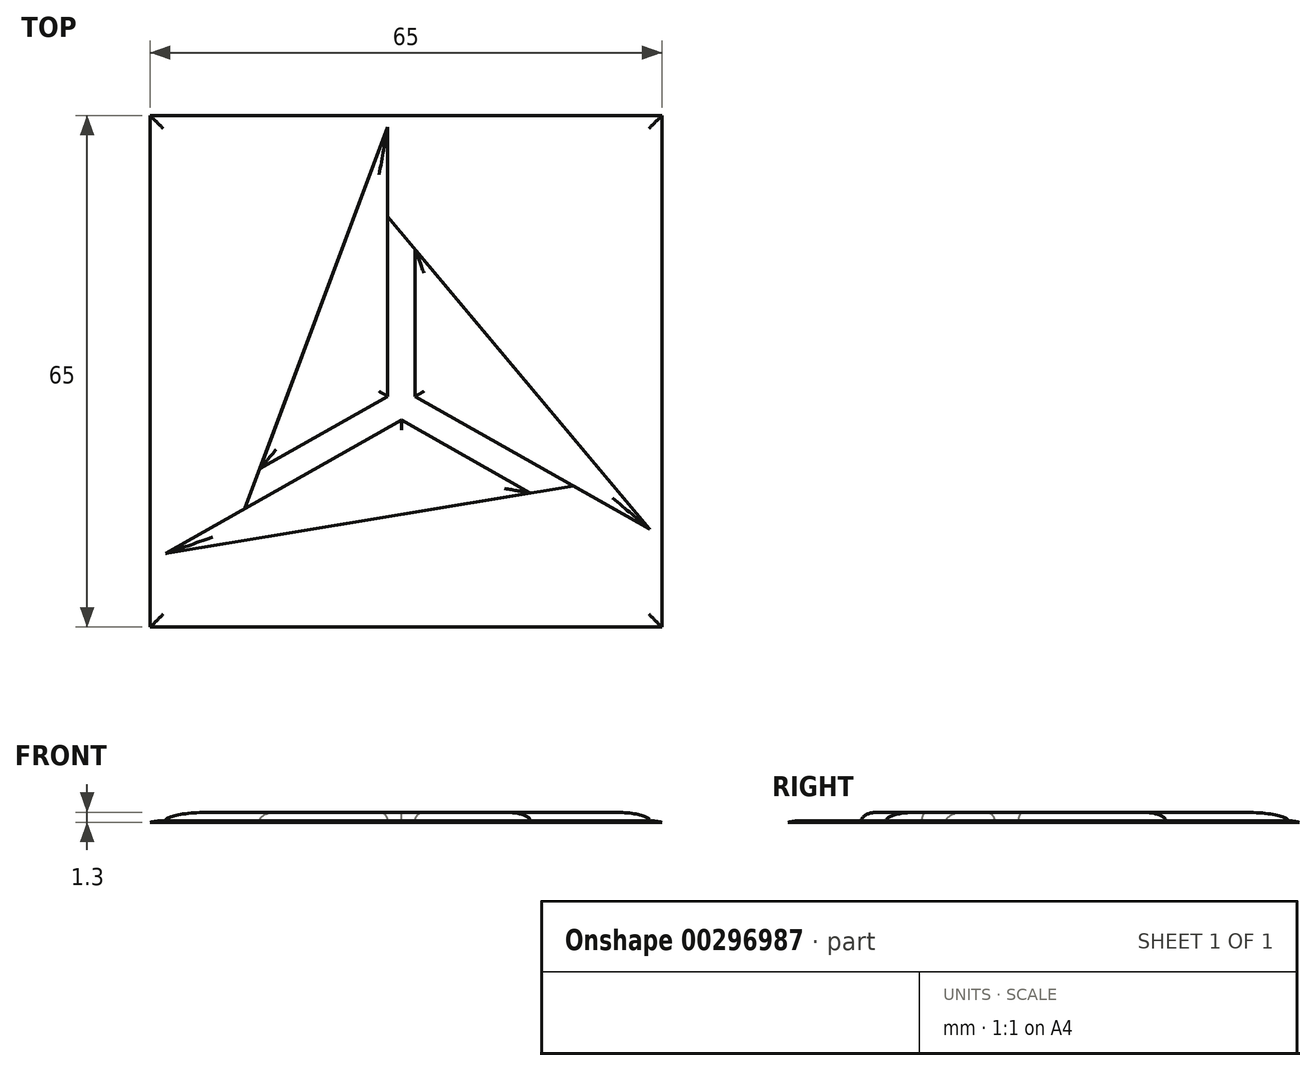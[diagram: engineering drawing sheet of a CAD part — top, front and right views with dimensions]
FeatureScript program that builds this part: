
annotation { "Feature Type Name" : "Feature", "Feature Type Description" : "" }
export const myFeature = defineFeature(function(context is Context, id is Id, definition is map)
    precondition{}
    {
        {
            var Q0;
            Q0=qCreatedBy(makeId("Top.planeOp"),FACE);
            var sketch = newSketch(context, id + "F0", { "sketchPlane" : qUnion([Q0])});
            skLineSegment(sketch, "E0.0", {"start": v(-40.27, 11.94) * mm, "end": v(-24.02, 55.35) * mm});
            skLineSegment(sketch, "E0.1", {"start": v(-24.02, 21.13) * mm, "end": v(-40.27, 11.94) * mm});
            skLineSegment(sketch, "E0.2", {"start": v(-24.02, 55.35) * mm, "end": v(-24.02, 21.13) * mm});
            skLineSegment(sketch, "E1.0", {"start": v(-20.52, 39.8) * mm, "end": v(9.26, 4.28) * mm});
            skLineSegment(sketch, "E1.1", {"start": v(-20.52, 21.13) * mm, "end": v(-20.52, 39.8) * mm});
            skLineSegment(sketch, "E1.2", {"start": v(9.26, 4.28) * mm, "end": v(-20.52, 21.13) * mm});
            skLineSegment(sketch, "E2.0", {"start": v(-5.92, 8.85) * mm, "end": v(-52.25, 1.13) * mm});
            skLineSegment(sketch, "E2.1", {"start": v(-22.27, 18.1) * mm, "end": v(-5.92, 8.85) * mm});
            skLineSegment(sketch, "E2.2", {"start": v(-52.25, 1.13) * mm, "end": v(-22.27, 18.1) * mm});
            skSolve(sketch);
        }
        {
            var Q0;
            Q0=qSketchRegion(id+"F0",true);
            extrude(context, id + "F1", {"entities" : qUnion([Q0]), "depth" : 1.3 * mm, "offsetDistance" : 25 * mm});
        }
        {
            var Q0;
            Q0=makeQuery(id+"F1.opExtrude","CAP_FACE",FACE,{"disambiguationData":[OSD([sQuery(id+"F0.wireOp",EDGE,"E0.0"),sQuery(id+"F0.wireOp",EDGE,"E0.1"),sQuery(id+"F0.wireOp",EDGE,"E0.2")])],"isStart":false});
            var Q1;
            Q1=makeQuery(id+"F1.opExtrude","CAP_FACE",FACE,{"disambiguationData":[OSD([sQuery(id+"F0.wireOp",EDGE,"E1.0"),sQuery(id+"F0.wireOp",EDGE,"E1.1"),sQuery(id+"F0.wireOp",EDGE,"E1.2")])],"isStart":false});
            var Q2;
            Q2=makeQuery(id+"F1.opExtrude","CAP_FACE",FACE,{"disambiguationData":[OSD([sQuery(id+"F0.wireOp",EDGE,"E2.0"),sQuery(id+"F0.wireOp",EDGE,"E2.1"),sQuery(id+"F0.wireOp",EDGE,"E2.2")])],"isStart":false});
            fillet(context, id + "F2", {"entities" : qUnion([Q0, Q1, Q2]), "radius" : 1.1 * mm, "tangentPropagation" : true, "allowEdgeOverflow" : false});
        }
        {
            var Q0;
            Q0=makeQuery(id+"F1.opExtrude","CAP_FACE",FACE,{"disambiguationData":[OSD([sQuery(id+"F0.wireOp",EDGE,"E1.0"),sQuery(id+"F0.wireOp",EDGE,"E1.1"),sQuery(id+"F0.wireOp",EDGE,"E1.2")])],"isStart":true});
            var sketch = newSketch(context, id + "F3", { "sketchPlane" : qUnion([Q0])});
            skLineSegment(sketch, "E3", {"start": v(9.26, -4.28) * mm, "end": v(-20.52, -39.8) * mm});
            skLineSegment(sketch, "E4", {"start": v(-20.52, -39.8) * mm, "end": v(-24.02, -43.97) * mm});
            skLineSegment(sketch, "E5", {"start": v(-24.02, -43.97) * mm, "end": v(-24.02, -55.35) * mm});
            skLineSegment(sketch, "E6", {"start": v(-24.02, -55.35) * mm, "end": v(-42.18, -6.82) * mm});
            skLineSegment(sketch, "E7", {"start": v(-42.18, -6.82) * mm, "end": v(-52.25, -1.13) * mm});
            skLineSegment(sketch, "E8", {"start": v(-52.25, -1.13) * mm, "end": v(-0.44, -9.76) * mm});
            skLineSegment(sketch, "E9", {"start": v(-0.44, -9.76) * mm, "end": v(9.26, -4.28) * mm});
            skSolve(sketch);
        }
        {
            var Q0;
            Q0=qSketchRegion(id+"F3",true);
            extrude(context, id + "F4", {"entities" : qUnion([Q0]), "oppositeDirection" : true, "depth" : 0.2 * mm, "offsetDistance" : 25 * mm});
        }
        {
            var Q0;
            Q0=qCreatedBy(makeId("Top.planeOp"),FACE);
            var sketch = newSketch(context, id + "F5", { "sketchPlane" : qUnion([Q0])});
            skLineSegment(sketch, "E10.bottom", {"start": v(-54.2, 56.8) * mm, "end": v(10.8, 56.8) * mm});
            skLineSegment(sketch, "E10.top", {"start": v(-54.2, -8.2) * mm, "end": v(10.8, -8.2) * mm});
            skLineSegment(sketch, "E10.left", {"start": v(-54.2, 56.8) * mm, "end": v(-54.2, -8.2) * mm});
            skLineSegment(sketch, "E10.right", {"start": v(10.8, 56.8) * mm, "end": v(10.8, -8.2) * mm});
            skSolve(sketch);
        }
        {
            var Q0;
            Q0 = qSketchRegion(id + "F5", true);
            extrude(context, id + "F6", {"entities" : qUnion([Q0]), "depth" : 0.2 * mm, "offsetDistance" : 25 * mm});
        }
        {
            var Q0;
            Q0=makeQuery(id+"F6.opExtrude","CAP_EDGE",EDGE,{"disambiguationData":[OSD([sQuery(id+"F5.wireOp",EDGE,"E10.top")])],"isStart":false});
            var Q1;
            Q1=makeQuery(id+"F6.opExtrude","CAP_EDGE",EDGE,{"disambiguationData":[OSD([sQuery(id+"F5.wireOp",EDGE,"E10.right")])],"isStart":false});
            var Q2;
            Q2=makeQuery(id+"F6.opExtrude","CAP_EDGE",EDGE,{"disambiguationData":[OSD([sQuery(id+"F5.wireOp",EDGE,"E10.left")])],"isStart":false});
            var Q3;
            Q3=makeQuery(id+"F6.opExtrude","CAP_EDGE",EDGE,{"disambiguationData":[OSD([sQuery(id+"F5.wireOp",EDGE,"E10.bottom")])],"isStart":false});
            fillet(context, id + "F7", {"entities" : qUnion([Q0, Q1, Q2, Q3]), "radius" : 7 * mm, "tangentPropagation" : true, "allowEdgeOverflow" : false});
        }
    });
